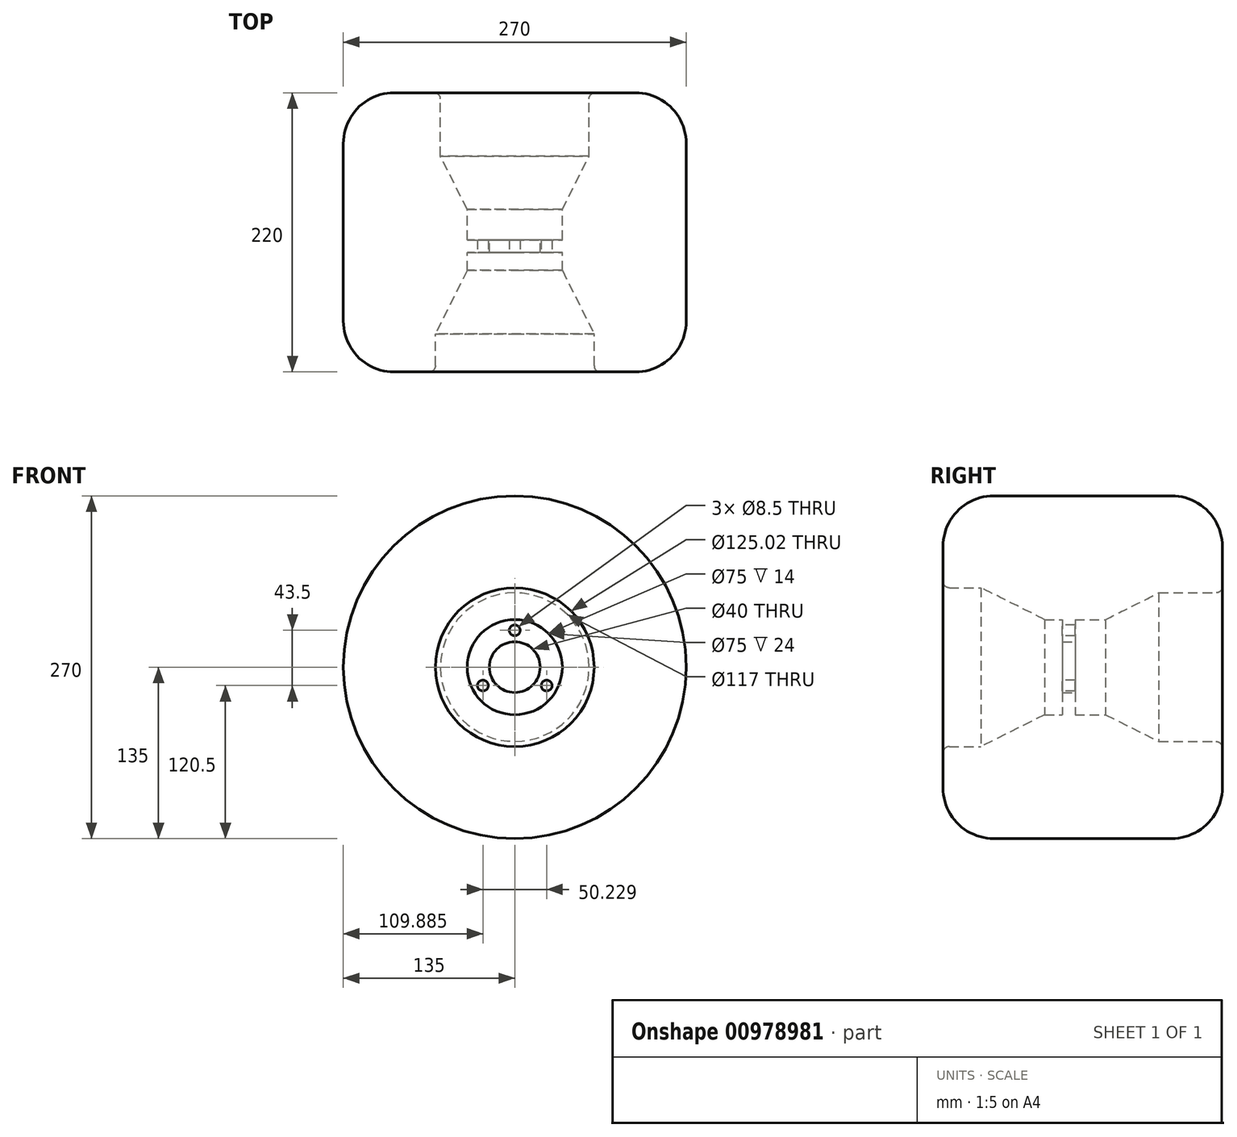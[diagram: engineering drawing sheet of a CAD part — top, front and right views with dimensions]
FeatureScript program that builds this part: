
annotation { "Feature Type Name" : "Feature", "Feature Type Description" : "" }
export const myFeature = defineFeature(function(context is Context, id is Id, definition is map)
    precondition{}
    {
        {
            var Q0;
            Q0=qCreatedBy(makeId("Right.planeOp"),FACE);
            var sketch = newSketch(context, id + "F0", { "sketchPlane" : qUnion([Q0])});
            skLineSegment(sketch, "E0", {"start": v(135.11, 0) * mm, "end": v(-127.68, 0) * mm, "construction": true});
            skLineSegment(sketch, "E1.top", {"start": v(-104.94, 135) * mm, "end": v(115.06, 135) * mm});
            skLineSegment(sketch, "E1.left", {"start": v(-104.94, 62.5) * mm, "end": v(-104.94, 135) * mm});
            skLineSegment(sketch, "E1.right", {"start": v(115.06, 58.5) * mm, "end": v(115.06, 135) * mm});
            skLineSegment(sketch, "E2", {"start": v(115.06, 58.5) * mm, "end": v(65.06, 58.5) * mm});
            skLineSegment(sketch, "E3", {"start": v(65.06, 58.5) * mm, "end": v(23.06, 37.5) * mm});
            skLineSegment(sketch, "E4", {"start": v(23.06, 37.5) * mm, "end": v(-0.94, 37.5) * mm});
            skLineSegment(sketch, "E5", {"start": v(-0.94, 37.5) * mm, "end": v(-0.94, 20) * mm});
            skLineSegment(sketch, "E6", {"start": v(-0.94, 20) * mm, "end": v(-10.94, 20) * mm});
            skLineSegment(sketch, "E7", {"start": v(-10.94, 20) * mm, "end": v(-10.94, 37.5) * mm});
            skLineSegment(sketch, "E8", {"start": v(-10.94, 37.5) * mm, "end": v(-24.94, 37.5) * mm});
            skLineSegment(sketch, "E9", {"start": v(-24.94, 37.5) * mm, "end": v(-74.94, 62.5) * mm});
            skLineSegment(sketch, "E10", {"start": v(-74.94, 62.5) * mm, "end": v(-104.94, 62.5) * mm});
            skPoint(sketch, "E1.bottom.start.orphan", {"position": v(-104.94, 0) * mm});
            skSolve(sketch);
        }
        {
            var Q0;
            Q0=makeQuery(id+"F0.imprint","IMPRINT",FACE,{"disambiguationData":[TD([[makeQuery(id+"F0.imprint","IMPRINT",EDGE,{"derivedFrom":sQuery(id+"F0.wireOp",EDGE,"E1.bottom")}),1.0]])]});
            var Q1;
            Q1=makeQuery(id+"F0.imprint","IMPRINT",FACE,{"disambiguationData":[TD([[makeQuery(id+"F0.imprint","IMPRINT",EDGE,{"derivedFrom":sQuery(id+"F0.wireOp",EDGE,"E1.top")}),-1.0]])]});
            var Q2;
            Q2=sQuery(id+"F0.wireOp",EDGE,"E0");
            revolve(context, id + "F1", {"surfaceOperationType" : NewSurfaceOperationType.NEW, "entities" : qUnion([Q0, Q1]), "axis" : qUnion([Q2]), "revolveType" : RevolveType.FULL});
        }
        {
            var Q0;
            Q0=makeQuery(id+"F1.opRevolve","SWEPT_EDGE",EDGE,{"disambiguationData":[OSD([sQuery(id+"F0.wireOp",EDGE,"E1.top"),sQuery(id+"F0.wireOp",EDGE,"E1.left")])]});
            var Q1;
            Q1=makeQuery(id+"F1.opRevolve","SWEPT_EDGE",EDGE,{"disambiguationData":[OSD([sQuery(id+"F0.wireOp",EDGE,"E1.top"),sQuery(id+"F0.wireOp",EDGE,"E1.right")])]});
            fillet(context, id + "F2", {"entities" : qUnion([Q0, Q1]), "radius" : 40 * mm, "tangentPropagation" : true, "allowEdgeOverflow" : false});
        }
        {
            var Q0;
            Q0=makeQuery(id+"F1.opRevolve","SWEPT_EDGE",EDGE,{"disambiguationData":[OSD([sQuery(id+"F0.wireOp",EDGE,"E1.left"),sQuery(id+"F0.wireOp",EDGE,"E10")])]});
            fillet(context, id + "F3", {"entities" : qUnion([Q0]), "radius" : 5 * mm, "tangentPropagation" : true, "allowEdgeOverflow" : false});
        }
        {
            var Q0;
            Q0=makeQuery(id+"F1.opRevolve","SWEPT_EDGE",EDGE,{"disambiguationData":[OSD([sQuery(id+"F0.wireOp",EDGE,"E1.right"),sQuery(id+"F0.wireOp",EDGE,"E2")])]});
            fillet(context, id + "F4", {"entities" : qUnion([Q0]), "radius" : 5 * mm, "tangentPropagation" : true, "allowEdgeOverflow" : false});
        }
        {
            var Q0;
            Q0=makeQuery(id+"F1.opRevolve","SWEPT_FACE",FACE,{"disambiguationData":[OSD([sQuery(id+"F0.wireOp",EDGE,"E7")])]});
            var sketch = newSketch(context, id + "F5", { "sketchPlane" : qUnion([Q0])});
            skCircle(sketch, "E11", {"center": v(0, 29) * mm, "radius": 4.25 * mm});
            skSolve(sketch);
        }
        {
            var Q0;
            Q0=makeQuery(id+"F5.imprint","IMPRINT",FACE,{"disambiguationData":[TD([[makeQuery(id+"F5.imprint","IMPRINT",EDGE,{"derivedFrom":sQuery(id+"F5.wireOp",EDGE,"E11")}),1.0]])]});
            var Q1;
            Q1=sQuery(id+"F5.wireOp",EDGE,"E11");
            var Q2;
            Q2=makeQuery(id+"F1.opRevolve","SWEPT_FACE",FACE,{"disambiguationData":[OSD([sQuery(id+"F0.wireOp",EDGE,"E5")])]});
            extrude(context, id + "F6", {"entities" : qUnion([Q0]), "operationType" : NewBodyOperationType.REMOVE, "surfaceEntities" : qUnion([Q1]), "endBound" : BoundingType.UP_TO_SURFACE, "oppositeDirection" : true, "depth" : 25 * mm, "endBoundEntityFace" : qUnion([Q2]), "offsetDistance" : 25 * mm});
        }
        {
            var Q0;
            Q0=makeQuery(id+"F1.opRevolve","SWEPT_BODY",BODY,{"disambiguationData":[OSD([sQuery(id+"F0.wireOp",EDGE,"E1.top"),sQuery(id+"F0.wireOp",EDGE,"E1.left"),sQuery(id+"F0.wireOp",EDGE,"E1.right"),sQuery(id+"F0.wireOp",EDGE,"E2"),sQuery(id+"F0.wireOp",EDGE,"E3"),sQuery(id+"F0.wireOp",EDGE,"E4"),sQuery(id+"F0.wireOp",EDGE,"E5"),sQuery(id+"F0.wireOp",EDGE,"E6"),sQuery(id+"F0.wireOp",EDGE,"E7"),sQuery(id+"F0.wireOp",EDGE,"E8"),sQuery(id+"F0.wireOp",EDGE,"E9"),sQuery(id+"F0.wireOp",EDGE,"E10")])]});
            var Q1;
            Q1=makeQuery(id+"F6.boolean.opBoolean","COPY",FACE,{"derivedFrom":makeQuery(id+"F6.opExtrude","SWEPT_FACE",FACE,{"disambiguationData":[OSD([sQuery(id+"F5.wireOp",EDGE,"E11")])]})});
            var Q2;
            Q2=sQuery(id+"F0.wireOp",EDGE,"E0");
            var Q3;
            Q3=makeQuery(id+"F1.opRevolve","SWEPT_BODY",BODY,{"disambiguationData":[OSD([sQuery(id+"F0.wireOp",EDGE,"E1.top"),sQuery(id+"F0.wireOp",EDGE,"E1.left"),sQuery(id+"F0.wireOp",EDGE,"E1.right"),sQuery(id+"F0.wireOp",EDGE,"E2"),sQuery(id+"F0.wireOp",EDGE,"E3"),sQuery(id+"F0.wireOp",EDGE,"E4"),sQuery(id+"F0.wireOp",EDGE,"E5"),sQuery(id+"F0.wireOp",EDGE,"E6"),sQuery(id+"F0.wireOp",EDGE,"E7"),sQuery(id+"F0.wireOp",EDGE,"E8"),sQuery(id+"F0.wireOp",EDGE,"E9"),sQuery(id+"F0.wireOp",EDGE,"E10")])]});
            circularPattern(context, id + "F7", {"patternType" : PatternType.FACE, "operationType" : NewBodyOperationType.REMOVE, "faces" : qUnion([Q1]), "axis" : qUnion([Q2]), "angle" : 360 * degree, "instanceCount" : 3, "equalSpace" : true});
        }
    });
